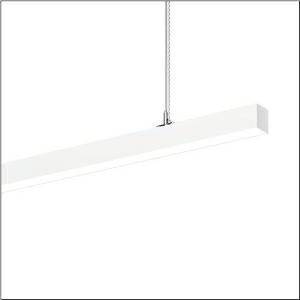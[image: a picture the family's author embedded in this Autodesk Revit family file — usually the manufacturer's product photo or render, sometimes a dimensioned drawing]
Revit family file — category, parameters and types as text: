
# Revit family: silica_r__21_51mx30tct9w_581c
name_source: partatom
category: Lighting Fixtures
units: mm (PartAtom-declared; Revit-internal decimal feet)

## family parameters
Cut with Voids When Loaded = No
Host = Face
Light Source = No
Part Type = Normal
Room Calculation Point = No
Round Connector Dimension = Use Diameter
Shared = No

## types (1)
- --- (1 x LED, 10300 lm, 84.4 W, 6500K)
    Apparent Load = 84 VA
    CIE Flux Codes = 47 79 96 58 100
    Color Rendering = 80
    Color Temperature = 6500K
    Default Elevation = 1800 mm
    Description = Silica® 21, office luminaire, primary optical cover: cover, of PMMA, opal, light emission: direct/indirect distribution, primary light characteristic: symmetric, installation type: suspended mounting, LED, rated luminous flux: 10.300lm, luminous efficacy: 116lm/W, light colour: 8tw, colour temperature: 2700..6500K, control gear: DALI DT8, with terminal, 3+2-pole, max. 2.5mm², mains connection: 220..240V, AC, 50/60Hz, rated input power: 88.7W, luminaire housing, of aluminium, traffic white (RAL 9016), length: 3.004mm, width: 53mm, height: 53mm, protection rating (complete): IP20, insulation class (complete): insulation class I (protective earthing), certification: CE, permissible operating ambient temperature: 0..+35°C, standard: EN 50419, packaging unit: 1 piece
    Height = 53 mm
    Lamp = 1 x LED
    Lamp Light Flux = 10300 lm
    Lamp Power = 84.4 W
    Lamp count = 1
    Length = 3004 mm
    Luminous efficacy = 122 lm/W
    Manufacturer = Siteco
    ModVariant = No
    Model = 51MX30TCT9W
    Mounting Place = Ceiling
    Mounting Type = Pendant
    Number of Poles = 1
    OnlyDefault = Yes
    Power Factor = 1
    Product Name = Silica® 21
    Product group = office luminaire | ceiling pendant
    ProductGroupID = 904
    Protection Class = Protection class I
    Protection Degree = IP 20
    RLX_Detail_Level = 1
    RLX_Emergency_Light_Flux = 0 lm
    RLX_Emergency_Type = 0
    RLX_Emergency_Type_DB = No
    RlxData = <blob elided: 17545 chars, md5=252523cf>
    Socket = socket
    Standby Power = 0 W
    System Light Flux = 10300 lm
    System Power = 84 W
    Type Comments = individual setting
    Type Image = l_1349023.jpg
    URL = http://relux.com
    VarID = @adj_139644
    Voltage = 0 V
    Weight = 0.00 kg
    Width = 53 mm

## geometry (parser evidence)
native form markers: Blend x4, Sweep x12
no freeform markers — native parametric forms only
